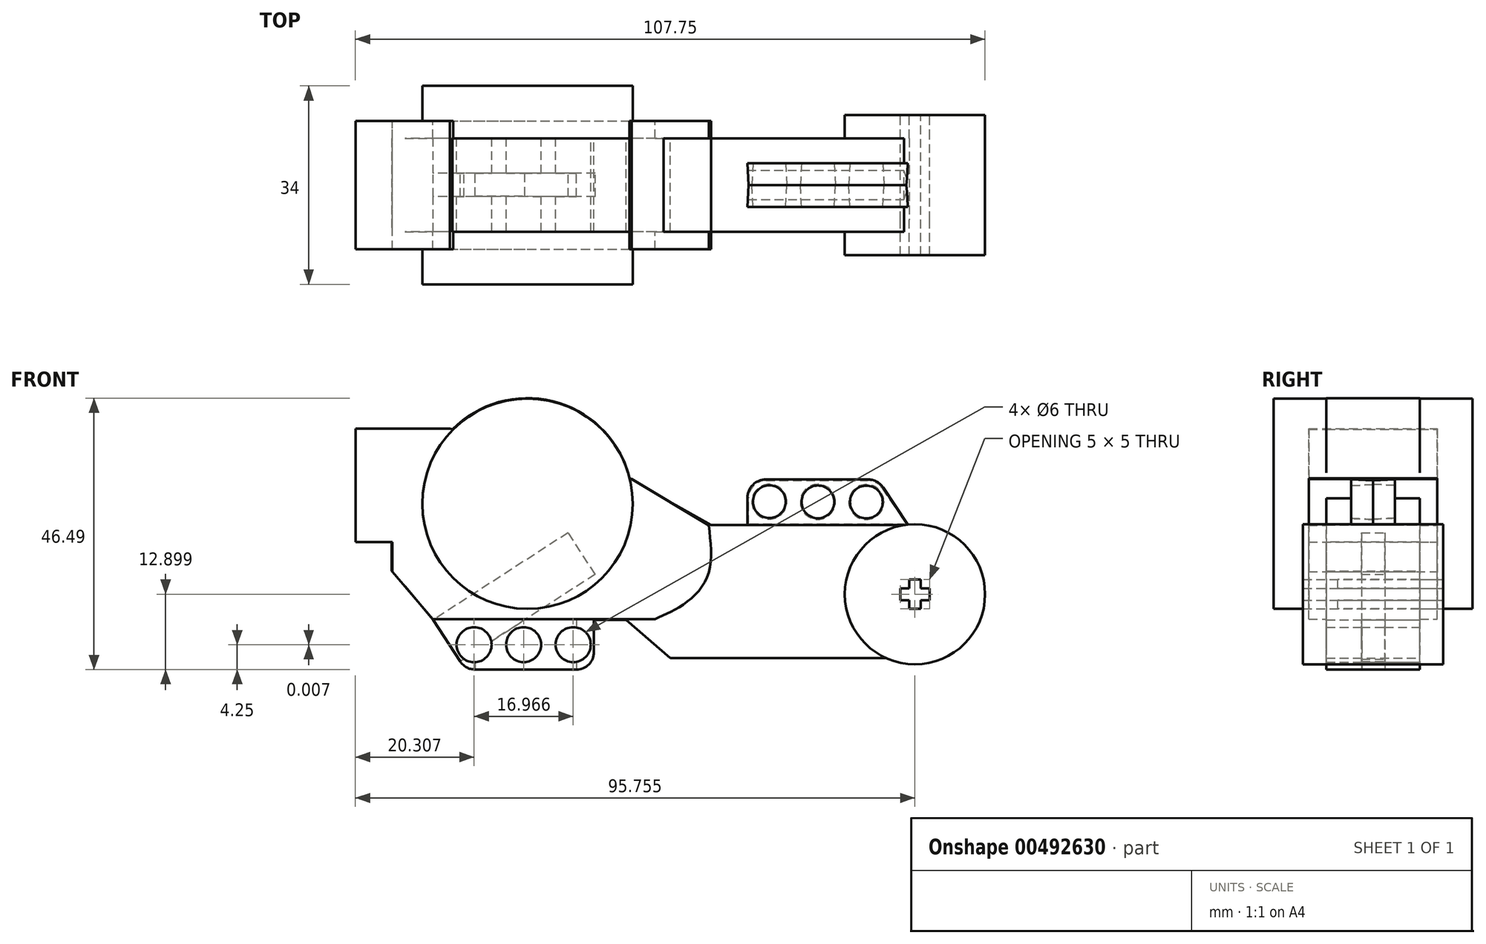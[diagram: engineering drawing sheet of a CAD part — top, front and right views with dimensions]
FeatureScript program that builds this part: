
annotation { "Feature Type Name" : "Feature", "Feature Type Description" : "" }
export const myFeature = defineFeature(function(context is Context, id is Id, definition is map)
    precondition{}
    {
        {
            var Q0;
            Q0=qCreatedBy(makeId("Front.planeOp"),FACE);
            var sketch = newSketch(context, id + "F0", { "sketchPlane" : qUnion([Q0])});
            skLineSegment(sketch, "E0.bottom", {"start": v(-61.94, 13.03) * mm, "end": v(45.81, 13.03) * mm, "construction": true});
            skLineSegment(sketch, "E0.top", {"start": v(-61.94, -32.57) * mm, "end": v(45.81, -32.57) * mm, "construction": true});
            skLineSegment(sketch, "E0.left", {"start": v(-61.94, 13.03) * mm, "end": v(-61.94, -32.57) * mm, "construction": true});
            skLineSegment(sketch, "E0.right", {"start": v(45.81, 13.03) * mm, "end": v(45.81, -32.57) * mm, "construction": true});
            skCircle(sketch, "E1", {"center": v(33.81, -21.62) * mm, "radius": 12 * mm});
            skLineSegment(sketch, "E2", {"start": v(31.94, -9.77) * mm, "end": v(-1.06, -9.77) * mm});
            skPoint(sketch, "E2.startSnap0", {"position": v(45.81, -9.77) * mm});
            skLineSegment(sketch, "E3", {"start": v(31.94, -32.57) * mm, "end": v(-8.06, -32.57) * mm});
            skLineSegment(sketch, "E4", {"start": v(-8.06, -32.57) * mm, "end": v(-15.62, -26.02) * mm});
            skLineSegment(sketch, "E5", {"start": v(-15.62, -26.02) * mm, "end": v(-48.62, -26.02) * mm});
            skLineSegment(sketch, "E6", {"start": v(-48.62, -26.02) * mm, "end": v(-55.72, -17.62) * mm});
            skLineSegment(sketch, "E7", {"start": v(-55.72, -17.62) * mm, "end": v(-55.72, -12.62) * mm});
            skPoint(sketch, "E8.endSnap0", {"position": v(-61.94, -9.77) * mm});
            skLineSegment(sketch, "E9", {"start": v(-55.72, -12.62) * mm, "end": v(-61.94, -12.62) * mm});
            skLineSegment(sketch, "E10", {"start": v(-61.94, -12.62) * mm, "end": v(-61.94, 6.38) * mm});
            skCircle(sketch, "E11", {"center": v(-32.5, -6.03) * mm, "radius": 18 * mm});
            skLineSegment(sketch, "E12", {"start": v(-1.06, -9.77) * mm, "end": v(-14.99, -1.9) * mm});
            skLineSegment(sketch, "E13", {"start": v(-61.94, 6.38) * mm, "end": v(-45.55, 6.38) * mm});
            skLineSegment(sketch, "E14", {"start": v(-42.65, -6.02) * mm, "end": v(39.6, -5.64) * mm, "construction": true});
            skLineSegment(sketch, "E15", {"start": v(-48.62, -26.02) * mm, "end": v(-21.12, -26.02) * mm});
            skLineSegment(sketch, "E16", {"start": v(-21.12, -26.02) * mm, "end": v(-21.12, -31.52) * mm});
            skLineSegment(sketch, "E17", {"start": v(-24.12, -34.52) * mm, "end": v(-41.48, -34.52) * mm});
            skLineSegment(sketch, "E18", {"start": v(-44, -33.15) * mm, "end": v(-48.62, -26.02) * mm});
            skLineSegment(sketch, "E19", {"start": v(-18.53, -30.26) * mm, "end": v(-50.9, -30.26) * mm, "construction": true});
            skCircle(sketch, "E20", {"center": v(-24.67, -30.26) * mm, "radius": 3 * mm});
            skCircle(sketch, "E21", {"center": v(-24.67, -30.26) * mm, "radius": 2.25 * mm});
            skCircle(sketch, "E22.1.0.0", {"center": v(-33.15, -30.27) * mm, "radius": 3 * mm});
            skCircle(sketch, "E22.2.0.0", {"center": v(-41.63, -30.27) * mm, "radius": 3 * mm});
            skLineSegment(sketch, "E22.direction1", {"start": v(-24.67, -30.26) * mm, "end": v(-33.15, -30.27) * mm, "construction": true});
            skCircle(sketch, "E23.1.0.0", {"center": v(-33.15, -30.26) * mm, "radius": 2.25 * mm});
            skCircle(sketch, "E23.2.0.0", {"center": v(-41.63, -30.26) * mm, "radius": 2.25 * mm});
            skLineSegment(sketch, "E23.direction1", {"start": v(-24.67, -30.26) * mm, "end": v(-33.15, -30.26) * mm, "construction": true});
            skPoint(sketch, "E24.visualSharp", {"position": v(-43.12, -34.52) * mm});
            skArc(sketch, "E24.filletArc", {"start": v(-44, -33.15) * mm, "mid": v(-42.92, -34.15) * mm, "end": v(-41.48, -34.52) * mm});
            skPoint(sketch, "E25.visualSharp", {"position": v(-21.12, -34.52) * mm});
            skArc(sketch, "E25.filletArc", {"start": v(-24.12, -34.52) * mm, "mid": v(-22, -33.64) * mm, "end": v(-21.12, -31.52) * mm});
            skSolve(sketch);
        }
        {
            var Q0;
            Q0 = qSketchRegion(id + "F0", true);
            var Q1;
            {var subQ0=sQuery(id+"F0.wireOp",EDGE,"E11");var subQ1=makeQuery(id+"F0.imprint","INTERSECT",VERTEX,{"derivedFrom":[subQ0,sQuery(id+"F0.wireOp",EDGE,"E12")]});Q1=makeQuery(id+"F0.imprint","IMPRINT",FACE,{"disambiguationData":[TD([[makeQuery(id+"F0.imprint","IMPRINT",EDGE,{"disambiguationData":[TD([[subQ1,-1.0]])],"derivedFrom":subQ0}),1.0]])]});}
            extrude(context, id + "F1", {"entities" : qUnion([Q0, Q1]), "endBound" : BoundingType.SYMMETRIC, "depth" : 16 * mm, "offsetDistance" : 25 * mm});
        }
        {
            var Q0;
            Q0=makeQuery(id+"F1.opExtrude","CAP_FACE",FACE,{"disambiguationData":[OSD([sQuery(id+"F0.wireOp",EDGE,"E0.bottom"),sQuery(id+"F0.wireOp",EDGE,"E0.top"),sQuery(id+"F0.wireOp",EDGE,"E0.left"),sQuery(id+"F0.wireOp",EDGE,"E0.right"),sQuery(id+"F0.wireOp",EDGE,"E1"),sQuery(id+"F0.wireOp",EDGE,"E3"),sQuery(id+"F0.wireOp",EDGE,"E10")])],"isStart":false});
            var sketch = newSketch(context, id + "F2", { "sketchPlane" : qUnion([Q0])});
            skLineSegment(sketch, "E26", {"start": v(-48.68, -25.88) * mm, "end": v(-10.68, -25.88) * mm});
            skFitSpline(sketch, "E27", {"points": [v(-10.68, -25.88) * mm, v(-6.04, -23.52) * mm, v(-1.64, -18.44) * mm, v(-1.49, -9.81) * mm], "startDerivative": vector(15.76, 6.76) * mm, "endDerivative": vector(-2.98, 24.56) * mm});
            skLineSegment(sketch, "E28", {"start": v(-1.49, -9.81) * mm, "end": v(-14.68, -1.86) * mm});
            skLineSegment(sketch, "E29", {"start": v(-48.68, -25.88) * mm, "end": v(-55.62, -17.76) * mm});
            skLineSegment(sketch, "E30", {"start": v(-55.62, -17.76) * mm, "end": v(-55.62, -12.69) * mm});
            skLineSegment(sketch, "E31", {"start": v(-55.62, -12.69) * mm, "end": v(-61.94, -12.69) * mm});
            skLineSegment(sketch, "E32", {"start": v(-61.94, -12.69) * mm, "end": v(-61.94, 6.77) * mm});
            skLineSegment(sketch, "E33", {"start": v(-61.94, 6.77) * mm, "end": v(-45.8, 6.77) * mm});
            skLineSegment(sketch, "E34", {"start": v(-45.8, 6.77) * mm, "end": v(-14.68, -1.86) * mm});
            skSolve(sketch);
        }
        {
            var Q0;
            Q0 = qSketchRegion(id + "F2", true);
            extrude(context, id + "F3", {"entities" : qUnion([Q0]), "operationType" : NewBodyOperationType.ADD, "depth" : 3 * mm, "offsetDistance" : 25 * mm, "hasSecondDirection" : true, "secondDirectionOppositeDirection" : true, "secondDirectionDepth" : 19 * mm});
        }
        {
            var Q0;
            Q0=makeQuery(id+"F1.opExtrude","CAP_FACE",FACE,{"disambiguationData":[OSD([sQuery(id+"F0.wireOp",EDGE,"E0.bottom"),sQuery(id+"F0.wireOp",EDGE,"E0.top"),sQuery(id+"F0.wireOp",EDGE,"E0.left"),sQuery(id+"F0.wireOp",EDGE,"E0.right"),sQuery(id+"F0.wireOp",EDGE,"E1"),sQuery(id+"F0.wireOp",EDGE,"E3"),sQuery(id+"F0.wireOp",EDGE,"E10")])],"isStart":false});
            var sketch = newSketch(context, id + "F4", { "sketchPlane" : qUnion([Q0])});
            skCircle(sketch, "E35", {"center": v(-32.48, -6.12) * mm, "radius": 18 * mm});
            skSolve(sketch);
        }
        {
            var Q0;
            Q0 = qSketchRegion(id + "F4", true);
            extrude(context, id + "F5", {"entities" : qUnion([Q0]), "operationType" : NewBodyOperationType.ADD, "depth" : 9 * mm, "offsetDistance" : 25 * mm, "hasSecondDirection" : true, "secondDirectionOppositeDirection" : true, "secondDirectionDepth" : 25 * mm});
        }
        {
            var Q0;
            {var subQ0=sQuery(id+"F0.wireOp",EDGE,"E3");var subQ1=sQuery(id+"F0.wireOp",EDGE,"E12");var subQ2=sQuery(id+"F0.wireOp",EDGE,"E6");var subQ3=sQuery(id+"F0.wireOp",EDGE,"E5");var subQ4=sQuery(id+"F0.wireOp",EDGE,"E1");var subQ5=sQuery(id+"F0.wireOp",EDGE,"E4");var subQ6=sQuery(id+"F0.wireOp",EDGE,"E2");Q0=makeQuery(id+"F3.boolean.opBoolean","SPLIT",FACE,{"disambiguationData":[TD([makeQuery(id+"F1.opExtrude","SWEPT_FACE",FACE,{"disambiguationData":[OSD([subQ4])]})])],"derivedFrom":makeQuery(id+"F1.opExtrude","CAP_FACE",FACE,{"disambiguationData":[OSD([subQ4,subQ6,subQ0,subQ5,subQ3,subQ2,sQuery(id+"F0.wireOp",EDGE,"E7"),sQuery(id+"F0.wireOp",EDGE,"E9"),sQuery(id+"F0.wireOp",EDGE,"E10"),sQuery(id+"F0.wireOp",EDGE,"E11"),subQ1,sQuery(id+"F0.wireOp",EDGE,"E13")])],"isStart":false})});}
            var sketch = newSketch(context, id + "F6", { "sketchPlane" : qUnion([Q0])});
            skCircle(sketch, "E36", {"center": v(33.81, -21.62) * mm, "radius": 12 * mm});
            skLineSegment(sketch, "E37", {"start": v(33.81, -24.12) * mm, "end": v(34.83, -24.12) * mm});
            skLineSegment(sketch, "E38", {"start": v(34.83, -24.12) * mm, "end": v(34.83, -19.12) * mm});
            skLineSegment(sketch, "E39", {"start": v(34.83, -19.12) * mm, "end": v(33.81, -19.12) * mm});
            skLineSegment(sketch, "E40", {"start": v(33.81, -19.12) * mm, "end": v(32.83, -19.12) * mm});
            skLineSegment(sketch, "E41", {"start": v(32.83, -19.12) * mm, "end": v(32.83, -24.12) * mm});
            skLineSegment(sketch, "E42", {"start": v(32.83, -24.12) * mm, "end": v(33.81, -24.12) * mm});
            skLineSegment(sketch, "E43", {"start": v(31.31, -21.62) * mm, "end": v(31.31, -20.62) * mm});
            skLineSegment(sketch, "E44", {"start": v(31.31, -20.62) * mm, "end": v(36.31, -20.62) * mm});
            skLineSegment(sketch, "E45", {"start": v(36.31, -20.62) * mm, "end": v(36.31, -21.62) * mm});
            skLineSegment(sketch, "E46", {"start": v(36.31, -21.62) * mm, "end": v(36.31, -22.62) * mm});
            skLineSegment(sketch, "E47", {"start": v(36.31, -22.62) * mm, "end": v(31.31, -22.62) * mm});
            skLineSegment(sketch, "E48", {"start": v(31.31, -22.62) * mm, "end": v(31.31, -21.62) * mm});
            skSolve(sketch);
        }
        {
            var Q0;
            Q0 = qSketchRegion(id + "F6", true);
            extrude(context, id + "F7", {"entities" : qUnion([Q0]), "operationType" : NewBodyOperationType.REMOVE, "oppositeDirection" : true, "depth" : 2 * mm, "offsetDistance" : 25 * mm});
        }
        {
            var Q0;
            {var subQ0=sQuery(id+"F6.wireOp",EDGE,"E47");var subQ1=sQuery(id+"F6.wireOp",EDGE,"E38");var subQ2=makeQuery(id+"F6.imprint","INTERSECT",VERTEX,{"derivedFrom":[subQ1,subQ0]});Q0=makeQuery(id+"F6.imprint","IMPRINT",FACE,{"disambiguationData":[TD([[makeQuery(id+"F6.imprint","IMPRINT",EDGE,{"disambiguationData":[TD([[subQ2,-1.0]])],"derivedFrom":subQ1}),1.0]])]});}
            var Q1;
            {var subQ6=sQuery(id+"F6.wireOp",EDGE,"E43");Q1=makeQuery(id+"F6.imprint","IMPRINT",FACE,{"disambiguationData":[TD([[makeQuery(id+"F6.imprint","IMPRINT",EDGE,{"derivedFrom":subQ6}),-1.0]])]});}
            var Q2;
            {var subQ4=sQuery(id+"F6.wireOp",EDGE,"E39");Q2=makeQuery(id+"F6.imprint","IMPRINT",FACE,{"disambiguationData":[TD([[makeQuery(id+"F6.imprint","IMPRINT",EDGE,{"derivedFrom":subQ4}),1.0]])]});}
            var Q3;
            {var subQ1=sQuery(id+"F6.wireOp",EDGE,"E45");Q3=makeQuery(id+"F6.imprint","IMPRINT",FACE,{"disambiguationData":[TD([[makeQuery(id+"F6.imprint","IMPRINT",EDGE,{"derivedFrom":subQ1}),-1.0]])]});}
            var Q4;
            {var subQ5=sQuery(id+"F6.wireOp",EDGE,"E37");Q4=makeQuery(id+"F6.imprint","IMPRINT",FACE,{"disambiguationData":[TD([[makeQuery(id+"F6.imprint","IMPRINT",EDGE,{"derivedFrom":subQ5}),1.0]])]});}
            extrude(context, id + "F8", {"entities" : qUnion([Q0, Q1, Q2, Q3, Q4]), "operationType" : NewBodyOperationType.REMOVE, "oppositeDirection" : true, "depth" : 25 * mm, "offsetDistance" : 25 * mm});
        }
        {
            var Q0;
            Q0=makeQuery(id+"F7.boolean.opBoolean","COPY",FACE,{"derivedFrom":makeQuery(id+"F7.opExtrude","CAP_FACE",FACE,{"disambiguationData":[OSD([sQuery(id+"F6.wireOp",EDGE,"E36")])],"isStart":false})});
            var sketch = newSketch(context, id + "F9", { "sketchPlane" : qUnion([Q0])});
            skCircle(sketch, "E49", {"center": v(33.81, -21.62) * mm, "radius": 12 * mm});
            skLineSegment(sketch, "E50", {"start": v(34.81, -24.12) * mm, "end": v(34.81, -19.12) * mm});
            skLineSegment(sketch, "E51", {"start": v(32.81, -19.12) * mm, "end": v(32.81, -24.12) * mm});
            skLineSegment(sketch, "E52", {"start": v(31.31, -20.62) * mm, "end": v(36.31, -20.62) * mm});
            skLineSegment(sketch, "E53", {"start": v(36.31, -22.62) * mm, "end": v(31.31, -22.62) * mm});
            skLineSegment(sketch, "E54", {"start": v(32.81, -24.12) * mm, "end": v(34.81, -24.12) * mm});
            skLineSegment(sketch, "E55", {"start": v(36.31, -22.62) * mm, "end": v(36.31, -20.62) * mm});
            skLineSegment(sketch, "E56", {"start": v(34.81, -19.12) * mm, "end": v(32.81, -19.12) * mm});
            skLineSegment(sketch, "E57", {"start": v(31.31, -20.62) * mm, "end": v(31.31, -22.62) * mm});
            skSolve(sketch);
        }
        {
            var Q0;
            Q0 = qSketchRegion(id + "F9", true);
            extrude(context, id + "F10", {"entities" : qUnion([Q0]), "depth" : 6 * mm, "offsetDistance" : 25 * mm, "hasSecondDirection" : true, "secondDirectionOppositeDirection" : true, "secondDirectionDepth" : 18 * mm});
        }
        {
            var Q0;
            Q0=qCreatedBy(makeId("Front.planeOp"),FACE);
            var sketch = newSketch(context, id + "F11", { "sketchPlane" : qUnion([Q0])});
            skLineSegment(sketch, "E58", {"start": v(32.33, -9.64) * mm, "end": v(5.33, -9.64) * mm});
            skLineSegment(sketch, "E59", {"start": v(5.33, -9.64) * mm, "end": v(5.33, -5.14) * mm});
            skLineSegment(sketch, "E60", {"start": v(8.33, -2.14) * mm, "end": v(25.73, -2.14) * mm});
            skLineSegment(sketch, "E61", {"start": v(28.23, -3.47) * mm, "end": v(32.33, -9.64) * mm});
            skLineSegment(sketch, "E62", {"start": v(2.55, -5.77) * mm, "end": v(30.55, -5.77) * mm, "construction": true});
            skCircle(sketch, "E63", {"center": v(8.9, -5.77) * mm, "radius": 3 * mm});
            skCircle(sketch, "E64", {"center": v(8.9, -5.77) * mm, "radius": 2.25 * mm});
            skCircle(sketch, "E65.1.0.0", {"center": v(17.2, -5.8) * mm, "radius": 3 * mm});
            skCircle(sketch, "E65.2.0.0", {"center": v(25.5, -5.83) * mm, "radius": 3 * mm});
            skLineSegment(sketch, "E65.direction1", {"start": v(8.9, -5.77) * mm, "end": v(17.2, -5.8) * mm, "construction": true});
            skCircle(sketch, "E66.1.0.0", {"center": v(17.2, -5.8) * mm, "radius": 2.25 * mm});
            skCircle(sketch, "E66.2.0.0", {"center": v(25.5, -5.83) * mm, "radius": 2.25 * mm});
            skPoint(sketch, "E67.visualSharp", {"position": v(5.33, -2.14) * mm});
            skArc(sketch, "E67.filletArc", {"start": v(8.33, -2.14) * mm, "mid": v(6.21, -3.02) * mm, "end": v(5.33, -5.14) * mm});
            skPoint(sketch, "E68.visualSharp", {"position": v(27.33, -2.14) * mm});
            skArc(sketch, "E68.filletArc", {"start": v(28.23, -3.47) * mm, "mid": v(27.15, -2.5) * mm, "end": v(25.73, -2.14) * mm});
            skSolve(sketch);
        }
        {
            var Q0;
            Q0 = qSketchRegion(id + "F11", true);
            extrude(context, id + "F12", {"entities" : qUnion([Q0]), "operationType" : NewBodyOperationType.ADD, "endBound" : BoundingType.SYMMETRIC, "depth" : 7.5 * mm, "offsetDistance" : 25 * mm, "hasDraft" : true, "draftAngle" : 3 * degree});
        }
        {
            var Q0;
            Q0=makeQuery(id+"F1.opExtrude","SWEPT_FACE",FACE,{"disambiguationData":[OSD([sQuery(id+"F0.wireOp",EDGE,"E18")])]});
            var sketch = newSketch(context, id + "F13", { "sketchPlane" : qUnion([Q0])});
            skPoint(sketch, "E69.startSnap0", {"position": v(0, -5.56) * mm});
            skPoint(sketch, "E69.endSnap0", {"position": v(0, -17.5) * mm});
            skLineSegment(sketch, "E70", {"start": v(-43.12, -17.5) * mm, "end": v(-43.12, -5.56) * mm});
            skLineSegment(sketch, "E71.MirrorCS", {"start": v(-43.12, 2) * mm, "end": v(-21.12, 2) * mm});
            skLineSegment(sketch, "E72", {"start": v(-2, -5.56) * mm, "end": v(-2, 4.57) * mm});
            skLineSegment(sketch, "E73.MirrorCS", {"start": v(2, -5.56) * mm, "end": v(2, 4.57) * mm});
            skSolve(sketch);
        }
        {
            var Q0;
            {var subQ0=sQuery(id+"F13.wireOp",EDGE,"E72");Q0=makeQuery(id+"F13.imprint","IMPRINT",FACE,{"disambiguationData":[TD([[makeQuery(id+"F13.imprint","IMPRINT",EDGE,{"derivedFrom":subQ0}),-1.0]])]});}
            extrude(context, id + "F14", {"entities" : qUnion([Q0]), "operationType" : NewBodyOperationType.REMOVE, "oppositeDirection" : true, "depth" : 27.5 * mm, "offsetDistance" : 25 * mm});
        }
        {
            var Q0;
            Q0=makeQuery(id+"F1.opExtrude","SWEPT_FACE",FACE,{"disambiguationData":[OSD([sQuery(id+"F0.wireOp",EDGE,"E17")])]});
            var sketch = newSketch(context, id + "F15", { "sketchPlane" : qUnion([Q0])});
            skLineSegment(sketch, "E74", {"start": v(-22, -2) * mm, "end": v(-44, -2) * mm});
            skLineSegment(sketch, "E75.MirrorCS", {"start": v(-21.12, 2) * mm, "end": v(-45.22, 1.87) * mm});
            skSolve(sketch);
        }
        {
            var Q0;
            {var subQ0=sQuery(id+"F15.wireOp",EDGE,"E74");Q0=makeQuery(id+"F15.imprint","IMPRINT",FACE,{"disambiguationData":[TD([[makeQuery(id+"F15.imprint","IMPRINT",EDGE,{"derivedFrom":subQ0}),-1.0]])]});}
            extrude(context, id + "F16", {"entities" : qUnion([Q0]), "operationType" : NewBodyOperationType.REMOVE, "oppositeDirection" : true, "depth" : 8.5 * mm, "offsetDistance" : 25 * mm});
        }
    });
